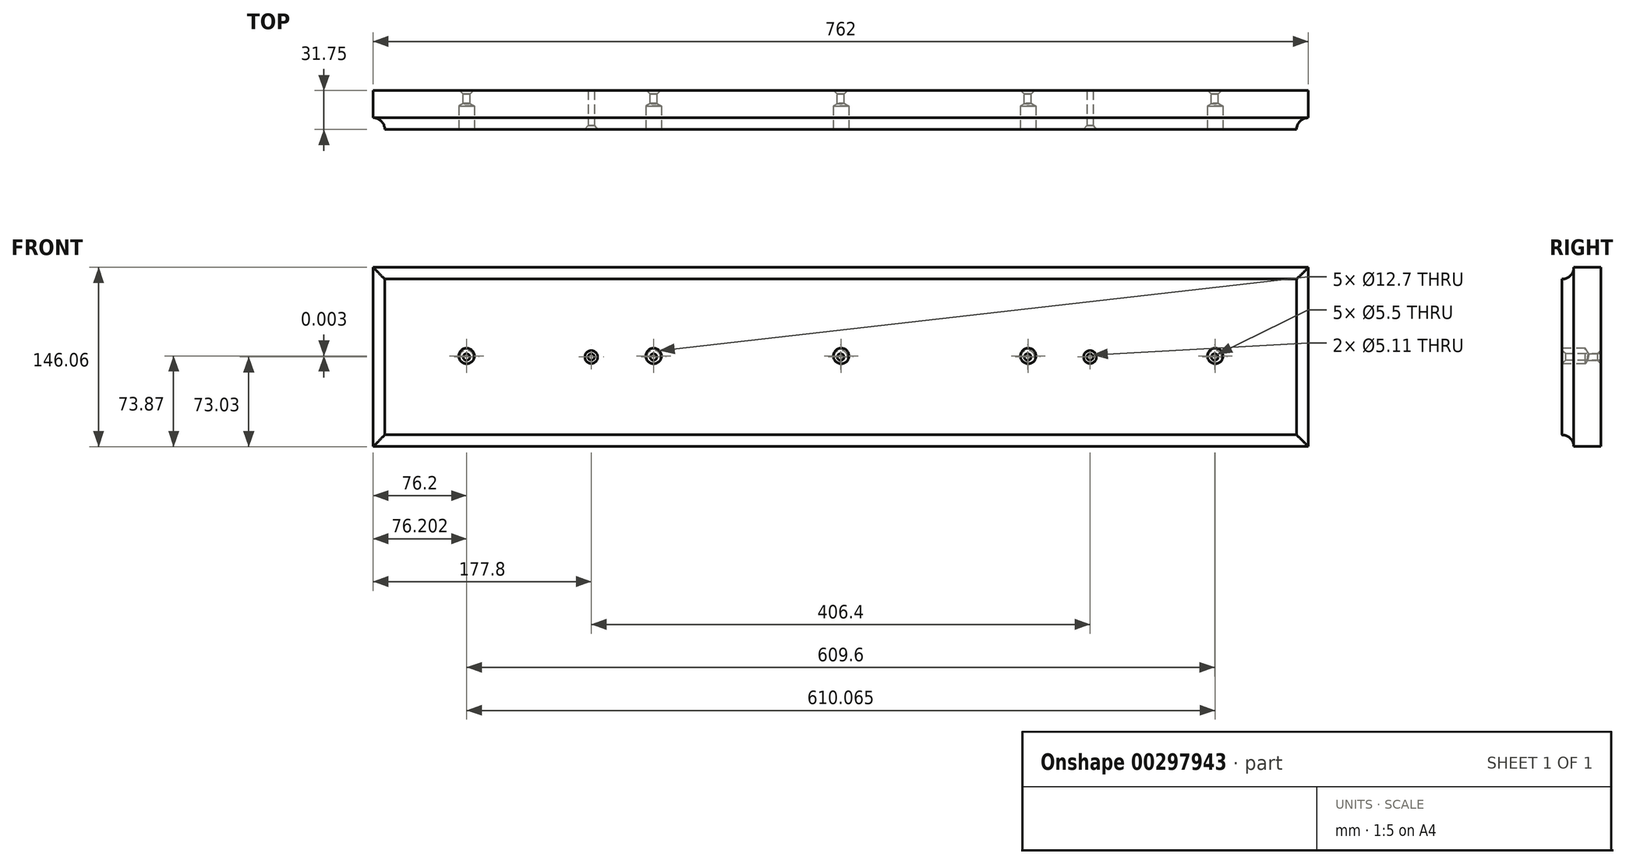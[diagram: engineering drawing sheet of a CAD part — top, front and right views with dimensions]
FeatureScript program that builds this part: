
annotation { "Feature Type Name" : "Feature", "Feature Type Description" : "" }
export const myFeature = defineFeature(function(context is Context, id is Id, definition is map)
    precondition{}
    {
        {
            var Q0;
            Q0=qCreatedBy(makeId("Front.planeOp"),FACE);
            var sketch = newSketch(context, id + "F0", { "sketchPlane" : qUnion([Q0])});
            skLineSegment(sketch, "E0.bottom", {"start": v(-381, 73.03) * mm, "end": v(381, 73.03) * mm});
            skLineSegment(sketch, "E0.top", {"start": v(-381, -73.03) * mm, "end": v(381, -73.03) * mm});
            skLineSegment(sketch, "E0.left", {"start": v(-381, 73.03) * mm, "end": v(-381, -73.03) * mm});
            skLineSegment(sketch, "E0.right", {"start": v(381, 73.03) * mm, "end": v(381, -73.03) * mm});
            skPoint(sketch, "E0.middle", {"position": v(0, 0) * mm});
            skLineSegment(sketch, "E1", {"start": v(0, 0) * mm, "end": v(152.4, 0) * mm, "construction": true});
            skLineSegment(sketch, "E2", {"start": v(152.4, 0) * mm, "end": v(304.8, 0) * mm, "construction": true});
            skLineSegment(sketch, "E3", {"start": v(0, 0) * mm, "end": v(-152.4, 0) * mm, "construction": true});
            skLineSegment(sketch, "E4", {"start": v(-152.4, 0) * mm, "end": v(-304.8, 0) * mm, "construction": true});
            skPoint(sketch, "E5", {"position": v(-304.8, 0) * mm});
            skPoint(sketch, "E6", {"position": v(-152.4, 0) * mm});
            skPoint(sketch, "E7", {"position": v(152.4, 0) * mm});
            skPoint(sketch, "E8", {"position": v(304.8, 0) * mm});
            skSolve(sketch);
        }
        {
            var Q0;
            Q0 = qSketchRegion(id + "F0", true);
            extrude(context, id + "F1", {"entities" : qUnion([Q0]), "depth" : 31.75 * mm});
        }
        {
            var Q0;
            Q0=makeQuery(id+"F1.opExtrude","SWEPT_FACE",FACE,{"disambiguationData":[OSD([sQuery(id+"F0.wireOp",EDGE,"E0.left")])]});
            var sketch = newSketch(context, id + "F2", { "sketchPlane" : qUnion([Q0])});
            skCircle(sketch, "E9", {"center": v(31.75, 73.02) * mm, "radius": 9.53 * mm});
            skSolve(sketch);
        }
        {
            var Q0;
            Q0 = qSketchRegion(id + "F2", true);
            extrude(context, id + "F3", {"entities" : qUnion([Q0]), "operationType" : NewBodyOperationType.REMOVE, "endBound" : BoundingType.THROUGH_ALL, "oppositeDirection" : true, "depth" : 25.4 * mm});
        }
        {
            var Q0;
            Q0=makeQuery(id+"F1.opExtrude","SWEPT_FACE",FACE,{"disambiguationData":[OSD([sQuery(id+"F0.wireOp",EDGE,"E0.bottom")])]});
            var sketch = newSketch(context, id + "F4", { "sketchPlane" : qUnion([Q0])});
            skCircle(sketch, "E10", {"center": v(-381, -31.73) * mm, "radius": 9.53 * mm});
            skSolve(sketch);
        }
        {
            var Q0;
            Q0 = qSketchRegion(id + "F4", true);
            extrude(context, id + "F5", {"entities" : qUnion([Q0]), "operationType" : NewBodyOperationType.REMOVE, "endBound" : BoundingType.THROUGH_ALL, "oppositeDirection" : true, "depth" : 25.4 * mm});
        }
        {
            var Q0;
            Q0=makeQuery(id+"F1.opExtrude","SWEPT_FACE",FACE,{"disambiguationData":[OSD([sQuery(id+"F0.wireOp",EDGE,"E0.right")])]});
            var sketch = newSketch(context, id + "F6", { "sketchPlane" : qUnion([Q0])});
            skCircle(sketch, "E11", {"center": v(-31.75, -73.02) * mm, "radius": 9.53 * mm});
            skSolve(sketch);
        }
        {
            var Q0;
            Q0 = qSketchRegion(id + "F6", true);
            extrude(context, id + "F7", {"entities" : qUnion([Q0]), "operationType" : NewBodyOperationType.REMOVE, "endBound" : BoundingType.THROUGH_ALL, "oppositeDirection" : true, "depth" : 25.4 * mm});
        }
        {
            var Q0;
            Q0=makeQuery(id+"F1.opExtrude","SWEPT_FACE",FACE,{"disambiguationData":[OSD([sQuery(id+"F0.wireOp",EDGE,"E0.top")])]});
            var sketch = newSketch(context, id + "F8", { "sketchPlane" : qUnion([Q0])});
            skCircle(sketch, "E12", {"center": v(381.03, 31.77) * mm, "radius": 9.52 * mm});
            skSolve(sketch);
        }
        {
            var Q0;
            Q0 = qSketchRegion(id + "F8", true);
            extrude(context, id + "F9", {"entities" : qUnion([Q0]), "operationType" : NewBodyOperationType.REMOVE, "endBound" : BoundingType.THROUGH_ALL, "oppositeDirection" : true, "depth" : 25.4 * mm});
        }
        {
            var Q0;
            Q0=makeQuery(id+"F1.opExtrude","CAP_FACE",FACE,{"disambiguationData":[OSD([sQuery(id+"F0.wireOp",EDGE,"E0.bottom"),sQuery(id+"F0.wireOp",EDGE,"E0.top"),sQuery(id+"F0.wireOp",EDGE,"E0.left"),sQuery(id+"F0.wireOp",EDGE,"E0.right")])],"isStart":false});
            var sketch = newSketch(context, id + "F10", { "sketchPlane" : qUnion([Q0])});
            skLineSegment(sketch, "E13", {"start": v(0.47, 0.84) * mm, "end": v(152.87, 0.84) * mm, "construction": true});
            skLineSegment(sketch, "E14", {"start": v(152.87, 0.84) * mm, "end": v(305.27, 0.84) * mm, "construction": true});
            skLineSegment(sketch, "E15", {"start": v(-152.4, 0.84) * mm, "end": v(-304.8, 0.84) * mm, "construction": true});
            skLineSegment(sketch, "E16", {"start": v(0, 0) * mm, "end": v(-152.4, 0.84) * mm, "construction": true});
            skSolve(sketch);
        }
        {
            var Q0;
            Q0=sQuery(id+"F10.wireOp",VERTEX,"E15.end");
            var Q1;
            Q1=sQuery(id+"F10.wireOp",VERTEX,"E15.start");
            var Q2;
            Q2=sQuery(id+"F10.wireOp",VERTEX,"E13.start");
            var Q3;
            Q3=sQuery(id+"F10.wireOp",VERTEX,"E14.start");
            var Q4;
            Q4=sQuery(id+"F10.wireOp",VERTEX,"E14.end");
            var Q5;
            Q5=makeQuery(id+"F1.opExtrude","SWEPT_BODY",BODY,{"disambiguationData":[OSD([sQuery(id+"F0.wireOp",EDGE,"E0.bottom"),sQuery(id+"F0.wireOp",EDGE,"E0.top"),sQuery(id+"F0.wireOp",EDGE,"E0.left"),sQuery(id+"F0.wireOp",EDGE,"E0.right")])]});
            hole(context, id + "F11", {"style" : HoleStyle.SIMPLE, "endStyle" : HoleEndStyle.BLIND, "holeDiameter" : 12.7 * mm, "holeDepth" : 19.05 * mm, "tappedDepth" : 12.7 * mm, "tapClearance" : 3, "locations" : qUnion([Q0, Q1, Q2, Q3, Q4]), "scope" : qUnion([Q5])});
        }
        {
            var Q0;
            Q0=sQuery(id+"F0.wireOp",VERTEX,"E8");
            var Q1;
            Q1=sQuery(id+"F0.wireOp",VERTEX,"E7");
            var Q2;
            Q2=sQuery(id+"F0.wireOp",VERTEX,"E0.middle");
            var Q3;
            Q3=sQuery(id+"F0.wireOp",VERTEX,"E6");
            var Q4;
            Q4=sQuery(id+"F0.wireOp",VERTEX,"E5");
            var Q5;
            Q5=makeQuery(id+"F1.opExtrude","SWEPT_BODY",BODY,{"disambiguationData":[OSD([sQuery(id+"F0.wireOp",EDGE,"E0.bottom"),sQuery(id+"F0.wireOp",EDGE,"E0.top"),sQuery(id+"F0.wireOp",EDGE,"E0.left"),sQuery(id+"F0.wireOp",EDGE,"E0.right")])]});
            hole(context, id + "F12", {"style" : HoleStyle.C_SINK, "endStyle" : HoleEndStyle.THROUGH, "oppositeDirection" : true, "holeDiameter" : 5.5 * mm, "cSinkDiameter" : 11.2 * mm, "cSinkAngle" : 90 * degree, "tappedDepth" : 12.7 * mm, "tapClearance" : 3, "locations" : qUnion([Q0, Q1, Q2, Q3, Q4]), "scope" : qUnion([Q5])});
        }
        {
            var Q0;
            Q0=makeQuery(id+"F1.opExtrude","CAP_FACE",FACE,{"disambiguationData":[OSD([sQuery(id+"F0.wireOp",EDGE,"E0.bottom"),sQuery(id+"F0.wireOp",EDGE,"E0.top"),sQuery(id+"F0.wireOp",EDGE,"E0.left"),sQuery(id+"F0.wireOp",EDGE,"E0.right")])],"isStart":false});
            var sketch = newSketch(context, id + "F13", { "sketchPlane" : qUnion([Q0])});
            skLineSegment(sketch, "E17", {"start": v(0, 0) * mm, "end": v(-203.2, 0) * mm, "construction": true});
            skLineSegment(sketch, "E18", {"start": v(0, 0) * mm, "end": v(203.2, 0) * mm, "construction": true});
            skPoint(sketch, "E19", {"position": v(-203.2, 0) * mm});
            skPoint(sketch, "E20", {"position": v(203.2, 0) * mm});
            skSolve(sketch);
        }
        {
            var Q0;
            Q0=sQuery(id+"F13.wireOp",VERTEX,"E19");
            var Q1;
            Q1=sQuery(id+"F13.wireOp",VERTEX,"E18.end");
            var Q2;
            Q2=makeQuery(id+"F1.opExtrude","SWEPT_BODY",BODY,{"disambiguationData":[OSD([sQuery(id+"F0.wireOp",EDGE,"E0.bottom"),sQuery(id+"F0.wireOp",EDGE,"E0.top"),sQuery(id+"F0.wireOp",EDGE,"E0.left"),sQuery(id+"F0.wireOp",EDGE,"E0.right")])]});
            hole(context, id + "F14", {"style" : HoleStyle.C_SINK, "endStyle" : HoleEndStyle.THROUGH, "standardTappedOrClearance" : lookupTablePath({ "standard" : "ANSI", "fit" : "Normal (ASME)", "size" : "#10", "type" : "Clearance" }), "standardBlindInLast" : lookupTablePath({ "fit" : "Free", "standard" : "ANSI", "size" : "#10", "type" : "Clearance" }), "holeDiameter" : 5.1 * mm, "cSinkDiameter" : 10.44 * mm, "cSinkAngle" : 82 * degree, "tappedDepth" : 12.7 * mm, "tapClearance" : 3, "locations" : qUnion([Q0, Q1]), "scope" : qUnion([Q2])});
        }
    });
